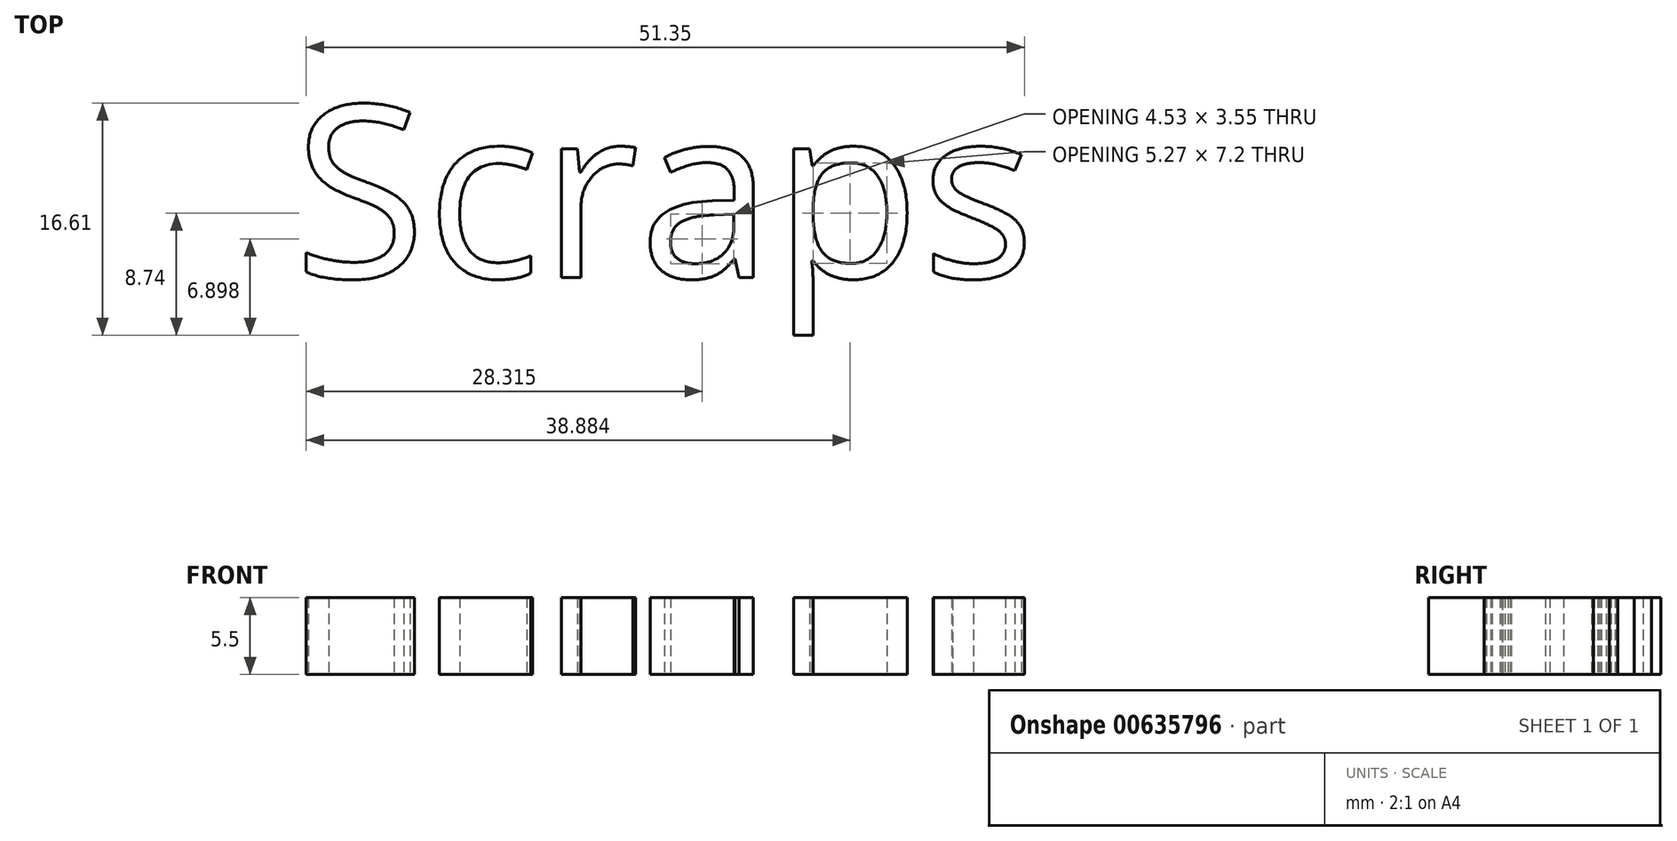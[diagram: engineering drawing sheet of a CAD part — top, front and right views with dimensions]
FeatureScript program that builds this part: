
annotation { "Feature Type Name" : "Feature", "Feature Type Description" : "" }
export const myFeature = defineFeature(function(context is Context, id is Id, definition is map)
    precondition{}
    {
        {
            var Q0;
            Q0=qCreatedBy(makeId("Top.planeOp"),FACE);
            var sketch = newSketch(context, id + "F0", { "sketchPlane" : qUnion([Q0])});
            skText(sketch, "E0", { "text": "Scraps", "fontName": "OpenSans-Regular.ttf"});
            const initialGuessF0  = {"E0": [-0.05424, 0.02688, 1, 0, 0.0124]};
            skSetInitialGuess(sketch, initialGuessF0);
            skSolve(sketch);
        }
        {
            var Q0;
            Q0 = qSketchRegion(id + "F0", true);
            extrude(context, id + "F1", {"entities" : qUnion([Q0]), "depth" : 5.5 * mm, "offsetDistance" : 25.4 * mm});
        }
    });
